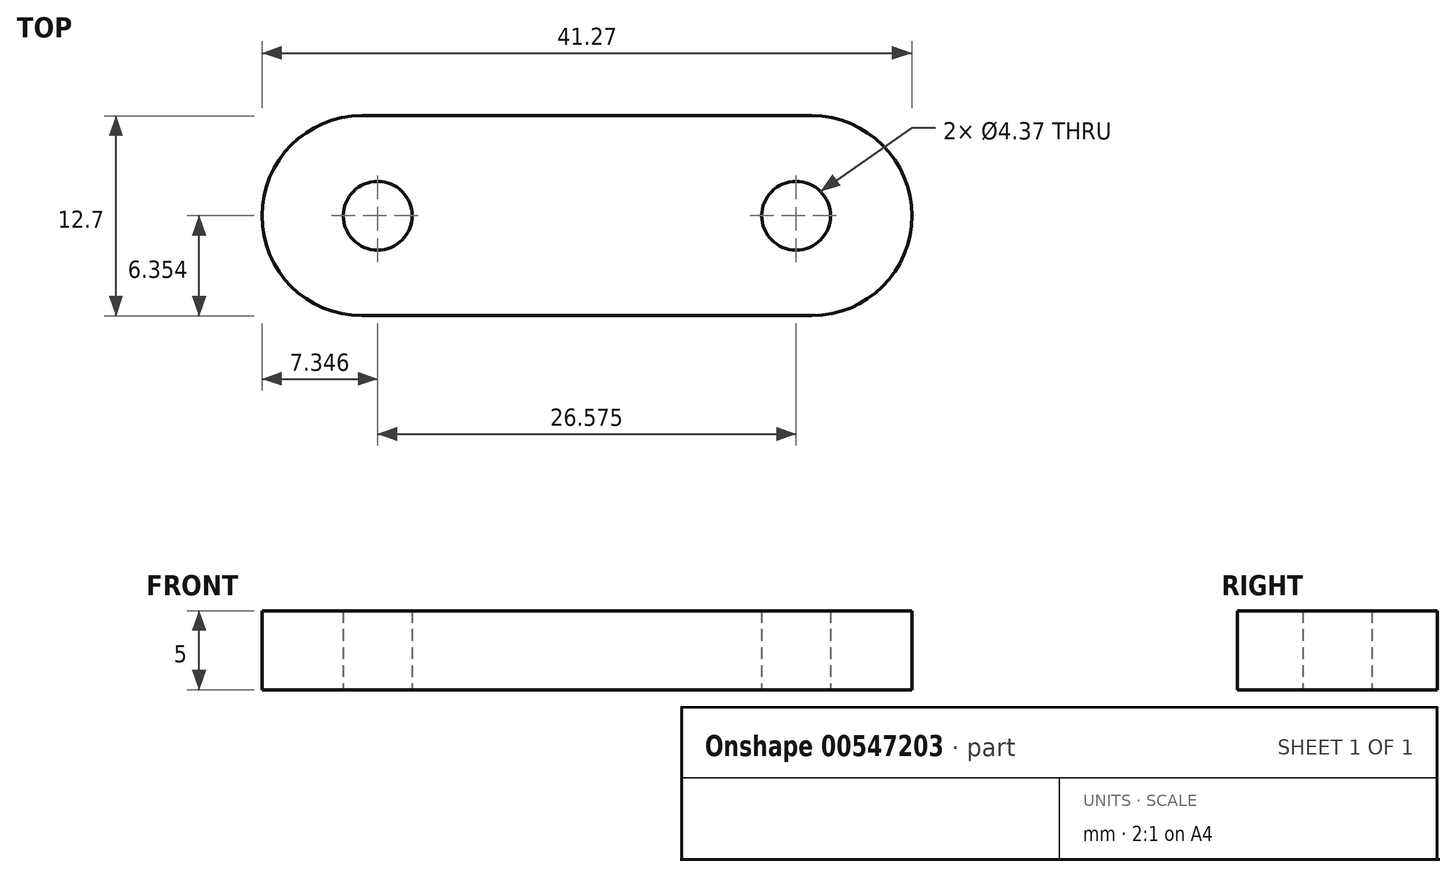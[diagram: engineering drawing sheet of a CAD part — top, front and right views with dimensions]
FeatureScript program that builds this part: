
annotation { "Feature Type Name" : "Feature", "Feature Type Description" : "" }
export const myFeature = defineFeature(function(context is Context, id is Id, definition is map)
    precondition{}
    {
        {
            var Q0;
            Q0=qCreatedBy(makeId("Top.planeOp"),FACE);
            var sketch = newSketch(context, id + "F0", { "sketchPlane" : qUnion([Q0])});
            skLineSegment(sketch, "E0.bottom", {"start": v(-19.9, 5.96) * mm, "end": v(21.38, 5.96) * mm});
            skLineSegment(sketch, "E0.top", {"start": v(-19.9, -6.74) * mm, "end": v(21.38, -6.74) * mm});
            skLineSegment(sketch, "E0.left", {"start": v(-19.9, 5.96) * mm, "end": v(-19.9, -6.74) * mm});
            skLineSegment(sketch, "E0.right", {"start": v(21.38, 5.96) * mm, "end": v(21.38, -6.74) * mm});
            skSolve(sketch);
        }
        {
            var Q0;
            Q0=qSketchRegion(id+"F0",true);
            extrude(context, id + "F1", {"entities" : qUnion([Q0]), "depth" : 5 * mm, "offsetDistance" : 25 * mm});
        }
        {
            var Q0;
            Q0=makeQuery(id+"F1.opExtrude","CAP_FACE",FACE,{"disambiguationData":[OSD([sQuery(id+"F0.wireOp",EDGE,"E0.bottom"),sQuery(id+"F0.wireOp",EDGE,"E0.top"),sQuery(id+"F0.wireOp",EDGE,"E0.left"),sQuery(id+"F0.wireOp",EDGE,"E0.right")])],"isStart":true});
            var sketch = newSketch(context, id + "F2", { "sketchPlane" : qUnion([Q0])});
            skCircle(sketch, "E1", {"center": v(-12.54, 0.39) * mm, "radius": 2.18 * mm});
            skCircle(sketch, "E2", {"center": v(14.03, 0.39) * mm, "radius": 2.18 * mm});
            skSolve(sketch);
        }
        {
            var Q0;
            Q0=qSketchRegion(id+"F2",true);
            extrude(context, id + "F3", {"entities" : qUnion([Q0]), "operationType" : NewBodyOperationType.REMOVE, "oppositeDirection" : true, "depth" : 25 * mm, "offsetDistance" : 25 * mm});
        }
        {
            var Q0;
            Q0=makeQuery(id+"F1.opExtrude","SWEPT_EDGE",EDGE,{"disambiguationData":[OSD([sQuery(id+"F0.wireOp",EDGE,"E0.top"),sQuery(id+"F0.wireOp",EDGE,"E0.right")])]});
            var Q1;
            Q1=makeQuery(id+"F1.opExtrude","SWEPT_EDGE",EDGE,{"disambiguationData":[OSD([sQuery(id+"F0.wireOp",EDGE,"E0.bottom"),sQuery(id+"F0.wireOp",EDGE,"E0.right")])]});
            var Q2;
            Q2=makeQuery(id+"F1.opExtrude","SWEPT_EDGE",EDGE,{"disambiguationData":[OSD([sQuery(id+"F0.wireOp",EDGE,"E0.top"),sQuery(id+"F0.wireOp",EDGE,"E0.left")])]});
            var Q3;
            Q3=makeQuery(id+"F1.opExtrude","SWEPT_EDGE",EDGE,{"disambiguationData":[OSD([sQuery(id+"F0.wireOp",EDGE,"E0.bottom"),sQuery(id+"F0.wireOp",EDGE,"E0.left")])]});
            fillet(context, id + "F4", {"entities" : qUnion([Q0, Q1, Q2, Q3]), "radius" : 6.35 * mm, "tangentPropagation" : true, "allowEdgeOverflow" : false});
        }
    });
